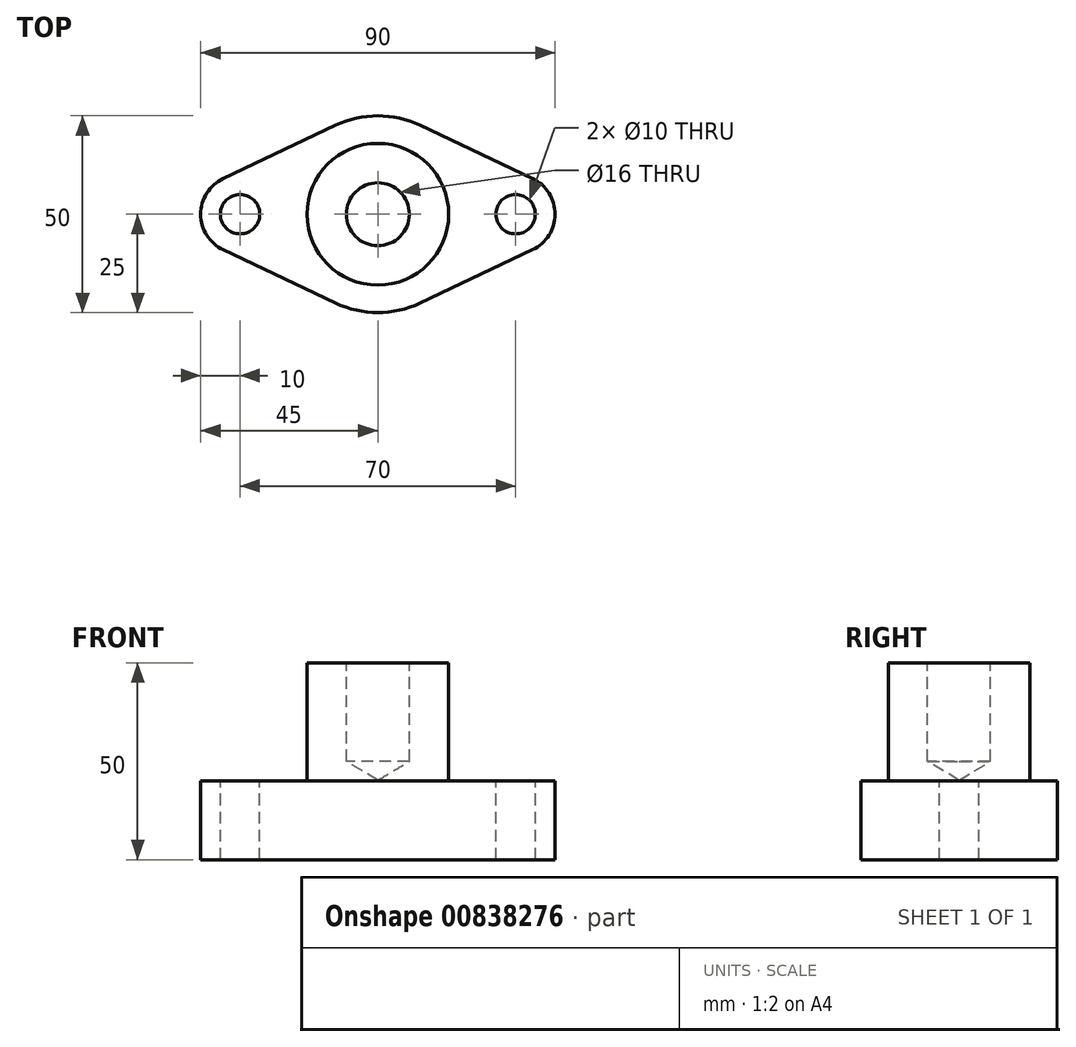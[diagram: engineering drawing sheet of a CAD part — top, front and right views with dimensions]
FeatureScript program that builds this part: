
annotation { "Feature Type Name" : "Feature", "Feature Type Description" : "" }
export const myFeature = defineFeature(function(context is Context, id is Id, definition is map)
    precondition{}
    {
        {
            var Q0;
            Q0=qCreatedBy(makeId("Top.planeOp"),FACE);
            var sketch = newSketch(context, id + "F0", { "sketchPlane" : qUnion([Q0])});
            skLineSegment(sketch, "E0", {"start": v(-39.29, 9.04) * mm, "end": v(-10.71, 22.59) * mm});
            skLineSegment(sketch, "E1", {"start": v(-39.29, -9.04) * mm, "end": v(-10.71, -22.59) * mm});
            skLineSegment(sketch, "E2", {"start": v(10.71, 22.59) * mm, "end": v(39.29, 9.04) * mm});
            skLineSegment(sketch, "E3", {"start": v(10.71, -22.59) * mm, "end": v(39.29, -9.04) * mm});
            skArc(sketch, "E4", {"start": v(-39.29, 9.04) * mm, "mid": v(-45, 0) * mm, "end": v(-39.29, -9.04) * mm});
            skArc(sketch, "E5", {"start": v(39.29, 9.04) * mm, "mid": v(45, 0) * mm, "end": v(39.29, -9.04) * mm});
            skArc(sketch, "E6", {"start": v(-10.71, 22.59) * mm, "mid": v(0, 25) * mm, "end": v(10.71, 22.59) * mm});
            skArc(sketch, "E7", {"start": v(-10.71, -22.59) * mm, "mid": v(0, -25) * mm, "end": v(10.71, -22.59) * mm});
            skSolve(sketch);
        }
        {
            var Q0;
            Q0=makeQuery(id+"F0.imprint","IMPRINT",FACE,{"disambiguationData":[TD([[makeQuery(id+"F0.imprint","IMPRINT",EDGE,{"derivedFrom":sQuery(id+"F0.wireOp",EDGE,"E0")}),-1.0]])]});
            extrude(context, id + "F1", {"entities" : qUnion([Q0]), "depth" : 20 * mm, "offsetDistance" : 25 * mm});
        }
        {
            var Q0;
            Q0=makeQuery(id+"F1.opExtrude","CAP_FACE",FACE,{"disambiguationData":[OSD([sQuery(id+"F0.wireOp",EDGE,"E0"),sQuery(id+"F0.wireOp",EDGE,"E1"),sQuery(id+"F0.wireOp",EDGE,"E2"),sQuery(id+"F0.wireOp",EDGE,"E3"),sQuery(id+"F0.wireOp",EDGE,"E4"),sQuery(id+"F0.wireOp",EDGE,"E5"),sQuery(id+"F0.wireOp",EDGE,"E6"),sQuery(id+"F0.wireOp",EDGE,"E7")])],"isStart":false});
            var sketch = newSketch(context, id + "F2", { "sketchPlane" : qUnion([Q0])});
            skPoint(sketch, "E8", {"position": v(-35, 0) * mm});
            skPoint(sketch, "E9", {"position": v(35, 0) * mm});
            skCircle(sketch, "E10", {"center": v(0, 0) * mm, "radius": 18 * mm});
            skSolve(sketch);
        }
        {
            var Q0;
            Q0=sQuery(id+"F2.wireOp",VERTEX,"E8");
            var Q1;
            Q1=sQuery(id+"F2.wireOp",VERTEX,"E9");
            var Q2;
            Q2=makeQuery(id+"F1.opExtrude","SWEPT_BODY",BODY,{"disambiguationData":[OSD([sQuery(id+"F0.wireOp",EDGE,"E0"),sQuery(id+"F0.wireOp",EDGE,"E1"),sQuery(id+"F0.wireOp",EDGE,"E2"),sQuery(id+"F0.wireOp",EDGE,"E3"),sQuery(id+"F0.wireOp",EDGE,"E4"),sQuery(id+"F0.wireOp",EDGE,"E5"),sQuery(id+"F0.wireOp",EDGE,"E6"),sQuery(id+"F0.wireOp",EDGE,"E7")])]});
            hole(context, id + "F3", {"style" : HoleStyle.SIMPLE, "endStyle" : HoleEndStyle.THROUGH, "holeDiameter" : 10 * mm, "majorDiameter" : 5 * mm, "isTappedThrough" : true, "tappedDepth" : 12 * mm, "tapClearance" : 3, "locations" : qUnion([Q0, Q1]), "scope" : qUnion([Q2])});
        }
        {
            var Q0;
            Q0=makeQuery(id+"F2.imprint","IMPRINT",FACE,{"disambiguationData":[TD([[makeQuery(id+"F2.imprint","IMPRINT",EDGE,{"derivedFrom":sQuery(id+"F2.wireOp",EDGE,"E10")}),1.0]])]});
            extrude(context, id + "F4", {"entities" : qUnion([Q0]), "operationType" : NewBodyOperationType.ADD, "depth" : 30 * mm, "offsetDistance" : 25 * mm});
        }
        {
            var Q0;
            Q0=makeQuery(id+"F4.opExtrude","CAP_FACE",FACE,{"disambiguationData":[OSD([sQuery(id+"F2.wireOp",EDGE,"E10")])],"isStart":false});
            var sketch = newSketch(context, id + "F5", { "sketchPlane" : qUnion([Q0])});
            skPoint(sketch, "E11", {"position": v(0, 0) * mm});
            skSolve(sketch);
        }
        {
            var Q0;
            Q0=sQuery(id+"F5.wireOp",VERTEX,"E11");
            var Q1;
            Q1=makeQuery(id+"F1.opExtrude","SWEPT_BODY",BODY,{"disambiguationData":[OSD([sQuery(id+"F0.wireOp",EDGE,"E0"),sQuery(id+"F0.wireOp",EDGE,"E1"),sQuery(id+"F0.wireOp",EDGE,"E2"),sQuery(id+"F0.wireOp",EDGE,"E3"),sQuery(id+"F0.wireOp",EDGE,"E4"),sQuery(id+"F0.wireOp",EDGE,"E5"),sQuery(id+"F0.wireOp",EDGE,"E6"),sQuery(id+"F0.wireOp",EDGE,"E7")])]});
            hole(context, id + "F6", {"style" : HoleStyle.SIMPLE, "endStyle" : HoleEndStyle.BLIND, "holeDiameter" : 16 * mm, "majorDiameter" : 5 * mm, "holeDepth" : 25 * mm, "isTappedThrough" : true, "tappedDepth" : 12 * mm, "tapClearance" : 3, "locations" : qUnion([Q0]), "scope" : qUnion([Q1])});
        }
    });
